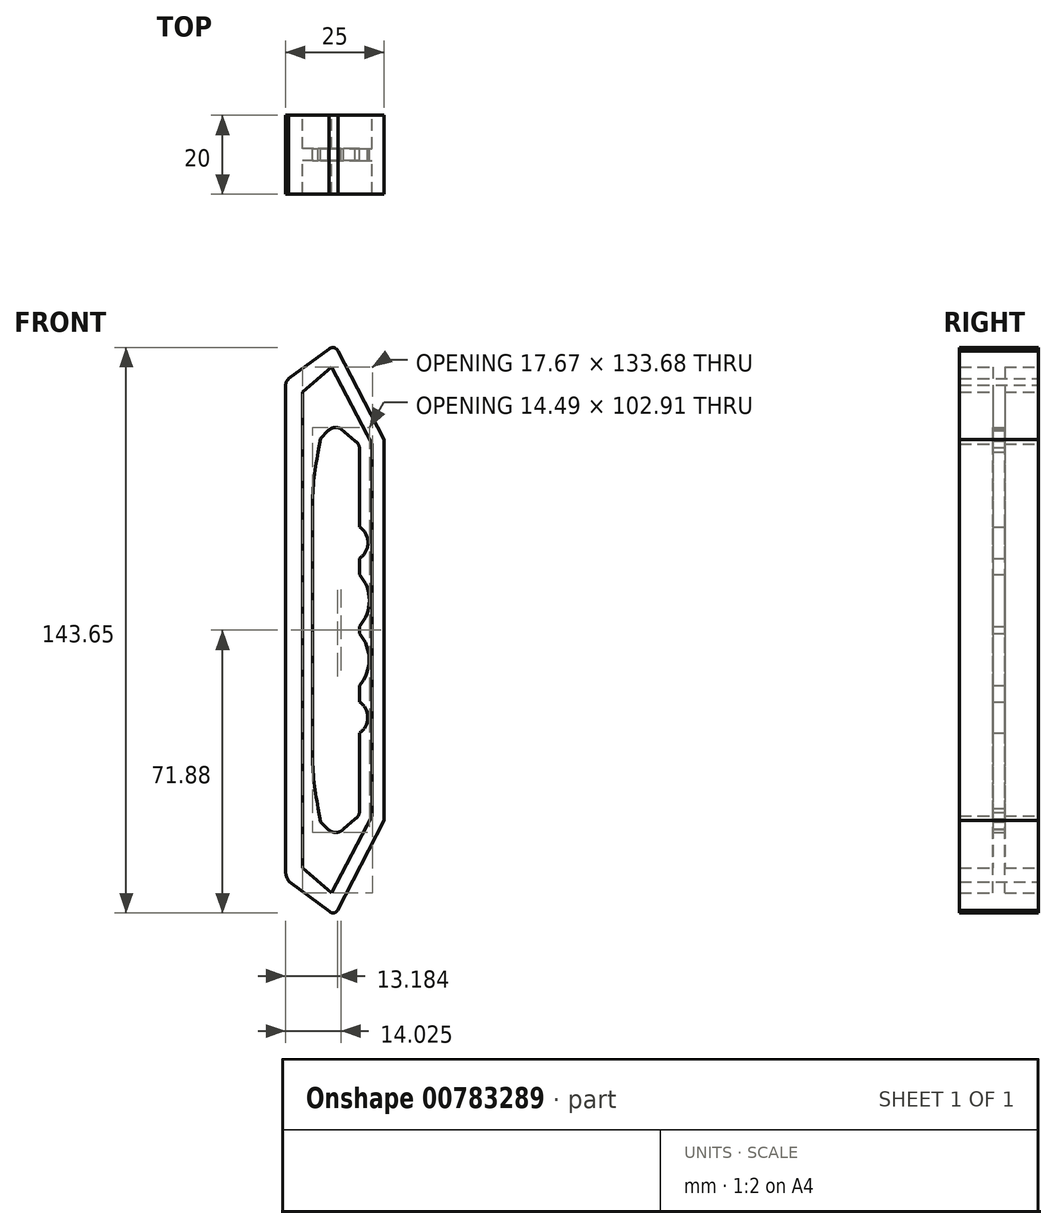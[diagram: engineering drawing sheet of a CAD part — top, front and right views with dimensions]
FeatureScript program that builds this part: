
annotation { "Feature Type Name" : "Feature", "Feature Type Description" : "" }
export const myFeature = defineFeature(function(context is Context, id is Id, definition is map)
    precondition{}
    {
        {
            var Q0;
            Q0=qCreatedBy(makeId("Front.planeOp"),FACE);
            var sketch = newSketch(context, id + "F0", { "sketchPlane" : qUnion([Q0])});
            skLineSegment(sketch, "E0.left", {"start": v(-14.1, 116.46) * mm, "end": v(-14.1, -7) * mm});
            skLineSegment(sketch, "E0.right", {"start": v(10.9, 102.65) * mm, "end": v(10.9, -18.25) * mm});
            skLineSegment(sketch, "E1", {"start": v(-0.76, 125.12) * mm, "end": v(10.9, 102.65) * mm});
            skLineSegment(sketch, "E2", {"start": v(-3.1, 125.65) * mm, "end": v(-13.32, 118.1) * mm});
            skLineSegment(sketch, "E3.MirrorCS", {"start": v(-0.94, -16.98) * mm, "end": v(10.9, 5.85) * mm});
            skLineSegment(sketch, "E4.MirrorCS", {"start": v(-2.95, -17.26) * mm, "end": v(-13.07, -9.79) * mm});
            skPoint(sketch, "E5.orphan", {"position": v(10.9, 126.75) * mm});
            skPoint(sketch, "E6.orphan", {"position": v(-14.1, 126.75) * mm});
            skPoint(sketch, "E7.orphan", {"position": v(-14.1, -18.25) * mm});
            skPoint(sketch, "E0.top.end.orphan", {"position": v(0, -18.25) * mm});
            skLineSegment(sketch, "E8", {"start": v(-2.41, 121.09) * mm, "end": v(-9.75, 114.7) * mm});
            skPoint(sketch, "E8.endSnap0", {"position": v(4.65, 114.7) * mm});
            skLineSegment(sketch, "E9", {"start": v(-9.75, 114.7) * mm, "end": v(-9.75, 54.25) * mm});
            skLineSegment(sketch, "E10", {"start": v(-2.41, 121.09) * mm, "end": v(7.92, 101.52) * mm});
            skLineSegment(sketch, "E11", {"start": v(7.92, 101.52) * mm, "end": v(7.92, 54.25) * mm});
            skLineSegment(sketch, "E12.MirrorCS", {"start": v(7.92, 6.98) * mm, "end": v(7.92, 54.25) * mm});
            skLineSegment(sketch, "E13.MirrorCS", {"start": v(-2.41, -12.59) * mm, "end": v(7.92, 6.98) * mm});
            skLineSegment(sketch, "E14.MirrorCS", {"start": v(-2.41, -12.59) * mm, "end": v(-9.75, -6.2) * mm});
            skLineSegment(sketch, "E15.MirrorCS", {"start": v(-9.75, -6.2) * mm, "end": v(-9.75, 54.25) * mm});
            skLineSegment(sketch, "E16", {"start": v(-7.32, 54.25) * mm, "end": v(-7.32, 84.48) * mm});
            skLineSegment(sketch, "E17", {"start": v(4.65, 93.25) * mm, "end": v(4.65, 83.46) * mm});
            skPoint(sketch, "E18.endSnap0", {"position": v(-9.75, 84.48) * mm});
            skPoint(sketch, "E19.orphan", {"position": v(4.65, 95.04) * mm});
            skLineSegment(sketch, "E20", {"start": v(4.65, 95.04) * mm, "end": v(4.65, 93.25) * mm});
            skArc(sketch, "E21.trimOffspring", {"start": v(-5.8, 99.53) * mm, "mid": v(-6.94, 92.04) * mm, "end": v(-7.32, 84.48) * mm});
            skPoint(sketch, "E22.orphan", {"position": v(0, 107.4) * mm});
            skLineSegment(sketch, "E23", {"start": v(-5.23, 102.94) * mm, "end": v(-5.8, 99.53) * mm});
            skLineSegment(sketch, "E24", {"start": v(4.65, 95.04) * mm, "end": v(4.65, 100.59) * mm});
            skLineSegment(sketch, "E25", {"start": v(3.6, 102.24) * mm, "end": v(0.02, 105.31) * mm});
            skLineSegment(sketch, "E26", {"start": v(-5.23, 102.94) * mm, "end": v(-3.21, 104.96) * mm});
            skArc(sketch, "E27", {"start": v(0.02, 105.31) * mm, "mid": v(-1.7, 105.69) * mm, "end": v(-3.27, 104.9) * mm});
            skArc(sketch, "E28", {"start": v(4.65, 100.59) * mm, "mid": v(4.31, 101.53) * mm, "end": v(3.6, 102.24) * mm});
            skLineSegment(sketch, "E29.trimOffspring", {"start": v(4.65, 72.47) * mm, "end": v(4.65, 68.38) * mm});
            skLineSegment(sketch, "E30", {"start": v(4.65, 83.46) * mm, "end": v(4.65, 80.44) * mm});
            skLineSegment(sketch, "E31.trimOffspring", {"start": v(4.65, 55.16) * mm, "end": v(4.65, 54.25) * mm});
            skLineSegment(sketch, "E32.MirrorCS", {"start": v(4.65, 53.34) * mm, "end": v(4.65, 54.25) * mm});
            skLineSegment(sketch, "E33.MirrorCS", {"start": v(4.65, 36.03) * mm, "end": v(4.65, 40.12) * mm});
            skLineSegment(sketch, "E34.MirrorCS", {"start": v(4.65, 25.04) * mm, "end": v(4.65, 28.06) * mm});
            skLineSegment(sketch, "E35.MirrorCS", {"start": v(4.65, 15.25) * mm, "end": v(4.65, 25.04) * mm});
            skLineSegment(sketch, "E36.MirrorCS", {"start": v(-7.32, 54.25) * mm, "end": v(-7.32, 24.02) * mm});
            skArc(sketch, "E37.MirrorCS", {"start": v(-5.8, 8.97) * mm, "mid": v(-6.94, 16.46) * mm, "end": v(-7.32, 24.02) * mm});
            skLineSegment(sketch, "E38.MirrorCS", {"start": v(-5.23, 5.56) * mm, "end": v(-6.72, 14.53) * mm});
            skPoint(sketch, "E39.orphan", {"position": v(-6.72, 93.97) * mm});
            skLineSegment(sketch, "E40.MirrorCS", {"start": v(-5.23, 5.56) * mm, "end": v(-3.21, 3.54) * mm});
            skArc(sketch, "E41.MirrorCS", {"start": v(0.64, 3.72) * mm, "mid": v(-1.29, 2.8) * mm, "end": v(-3.27, 3.6) * mm});
            skLineSegment(sketch, "E42.MirrorCS", {"start": v(3.6, 6.26) * mm, "end": v(0.64, 3.72) * mm});
            skPoint(sketch, "E43.MirrorP", {"position": v(4.65, 13.47) * mm});
            skLineSegment(sketch, "E44.MirrorCS", {"start": v(4.65, 13.47) * mm, "end": v(4.65, 7.91) * mm});
            skArc(sketch, "E45.MirrorCS", {"start": v(4.65, 7.91) * mm, "mid": v(4.31, 6.97) * mm, "end": v(3.6, 6.26) * mm});
            skLineSegment(sketch, "E46.MirrorCS", {"start": v(4.65, 13.47) * mm, "end": v(4.65, 15.25) * mm});
            skPoint(sketch, "E47.orphan", {"position": v(0.02, 3.19) * mm});
            skPoint(sketch, "E48.orphan", {"position": v(0.64, 104.78) * mm});
            skPoint(sketch, "E49.start.orphan", {"position": v(10.9, 54.25) * mm});
            skPoint(sketch, "E50.trimOffspring.end.orphan", {"position": v(-14.1, 54.25) * mm});
            skArc(sketch, "E51", {"start": v(4.65, 55.16) * mm, "mid": v(7.17, 61.77) * mm, "end": v(4.65, 68.38) * mm});
            skArc(sketch, "E52", {"start": v(4.65, 72.47) * mm, "mid": v(6.84, 76.46) * mm, "end": v(4.65, 80.44) * mm});
            skArc(sketch, "E53", {"start": v(4.65, 40.12) * mm, "mid": v(7.1, 46.73) * mm, "end": v(4.65, 53.34) * mm});
            skArc(sketch, "E54", {"start": v(4.65, 28.06) * mm, "mid": v(6.74, 32.05) * mm, "end": v(4.65, 36.03) * mm});
            skArc(sketch, "E55", {"start": v(-0.76, 125.12) * mm, "mid": v(-1.8, 125.98) * mm, "end": v(-3.1, 125.65) * mm});
            skArc(sketch, "E56", {"start": v(-13.32, 118.1) * mm, "mid": v(-13.88, 117.36) * mm, "end": v(-14.1, 116.46) * mm});
            skArc(sketch, "E57", {"start": v(-2.95, -17.26) * mm, "mid": v(-1.87, -17.62) * mm, "end": v(-0.94, -16.98) * mm});
            skArc(sketch, "E58", {"start": v(-14.1, -7) * mm, "mid": v(-13.83, -8.49) * mm, "end": v(-13.07, -9.79) * mm});
            skPoint(sketch, "E59.orphan", {"position": v(-1.6, 126.75) * mm});
            skSolve(sketch);
        }
        {
            var Q0;
            Q0 = qSketchRegion(id + "F0", true);
            extrude(context, id + "F1", {"entities" : qUnion([Q0]), "depth" : 10 * mm, "offsetDistance" : 25 * mm, "hasSecondDirection" : true, "secondDirectionOppositeDirection" : true, "secondDirectionDepth" : 10 * mm});
        }
        {
            var Q0;
            Q0=makeQuery(id+"F0.imprint","IMPRINT",FACE,{"disambiguationData":[TD([[makeQuery(id+"F0.imprint","IMPRINT",EDGE,{"derivedFrom":sQuery(id+"F0.wireOp",EDGE,"E8")}),1.0]])]});
            extrude(context, id + "F2", {"entities" : qUnion([Q0]), "operationType" : NewBodyOperationType.ADD, "depth" : 1.5 * mm, "offsetDistance" : 25 * mm, "hasSecondDirection" : true, "secondDirectionOppositeDirection" : true, "secondDirectionDepth" : 1.5 * mm});
        }
    });
